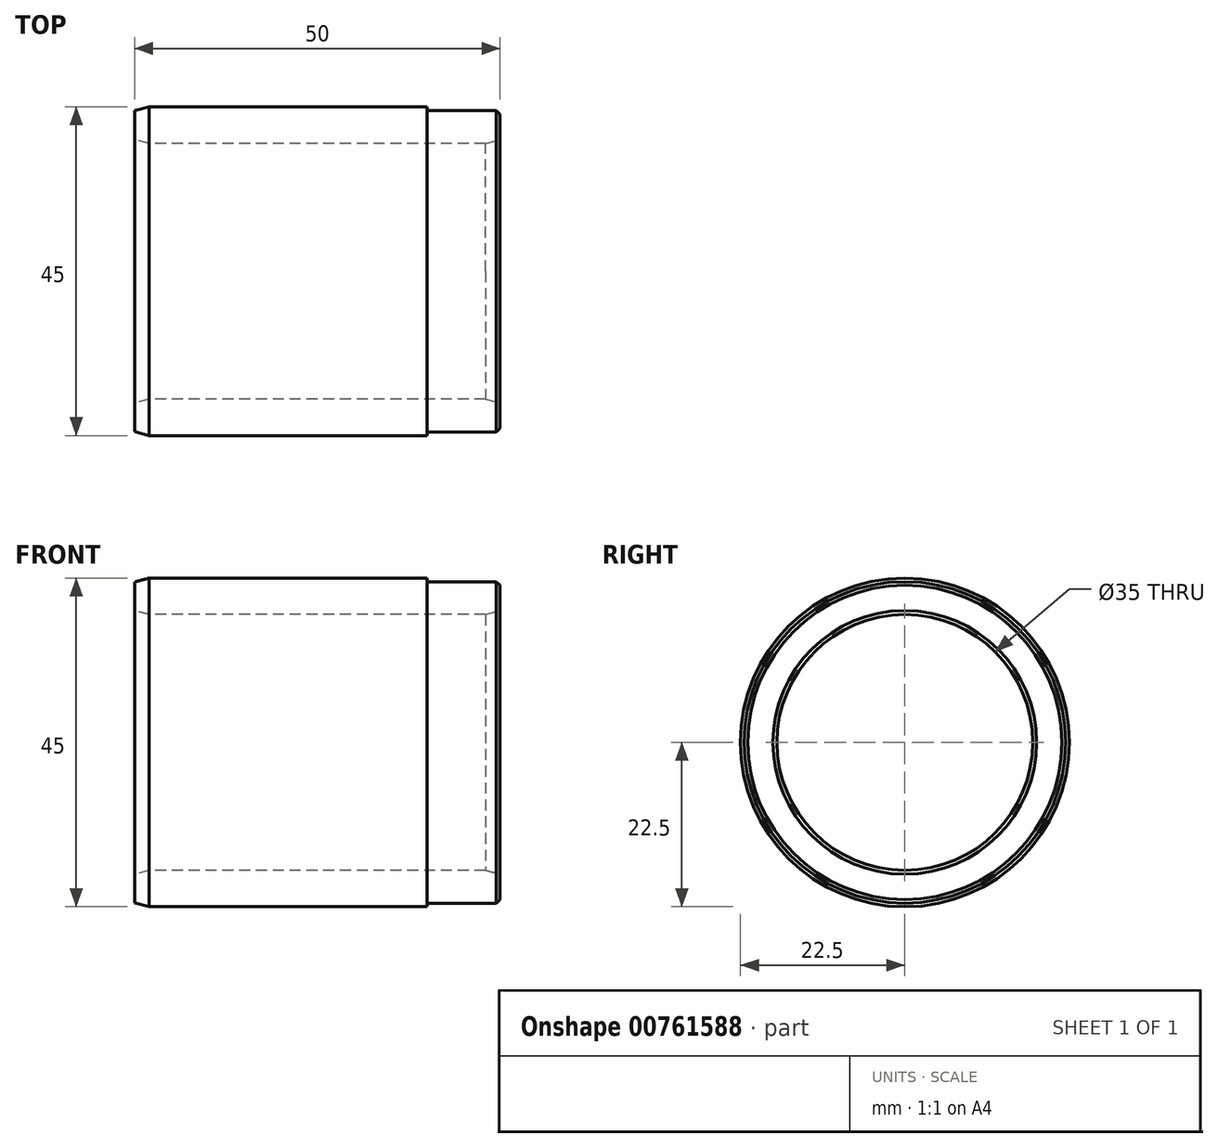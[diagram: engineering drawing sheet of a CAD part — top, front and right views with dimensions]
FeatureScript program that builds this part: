
annotation { "Feature Type Name" : "Feature", "Feature Type Description" : "" }
export const myFeature = defineFeature(function(context is Context, id is Id, definition is map)
    precondition{}
    {
        {
            var Q0;
            Q0=qCreatedBy(makeId("Front.planeOp"),FACE);
            var sketch = newSketch(context, id + "F0", { "sketchPlane" : qUnion([Q0])});
            skLineSegment(sketch, "E0", {"start": v(0, 17.5) * mm, "end": v(0, 22.5) * mm});
            skLineSegment(sketch, "E1", {"start": v(0, 22.5) * mm, "end": v(40, 22.5) * mm});
            skLineSegment(sketch, "E2", {"start": v(40, 22.5) * mm, "end": v(40, 22) * mm});
            skLineSegment(sketch, "E3", {"start": v(40, 22) * mm, "end": v(50, 22) * mm});
            skLineSegment(sketch, "E4", {"start": v(50, 22) * mm, "end": v(50, 17.5) * mm});
            skLineSegment(sketch, "E5", {"start": v(0, 17.5) * mm, "end": v(50, 17.5) * mm});
            skLineSegment(sketch, "E6", {"start": v(0, 0) * mm, "end": v(50, 0) * mm, "construction": true});
            skSolve(sketch);
        }
        {
            var Q0;
            Q0=makeQuery(id+"F0.imprint","IMPRINT",FACE,{"disambiguationData":[TD([[makeQuery(id+"F0.imprint","IMPRINT",EDGE,{"derivedFrom":sQuery(id+"F0.wireOp",EDGE,"E0")}),-1.0]])]});
            var Q1;
            Q1=sQuery(id+"F0.wireOp",EDGE,"E6");
            revolve(context, id + "F1", {"surfaceOperationType" : NewSurfaceOperationType.NEW, "entities" : qUnion([Q0]), "axis" : qUnion([Q1]), "revolveType" : RevolveType.FULL});
        }
        {
            var Q0;
            Q0=makeQuery(id+"F1.opRevolve","SWEPT_EDGE",EDGE,{"disambiguationData":[OSD([sQuery(id+"F0.wireOp",EDGE,"E0"),sQuery(id+"F0.wireOp",EDGE,"E1")])]});
            var Q1;
            Q1=makeQuery(id+"F1.opRevolve","SWEPT_EDGE",EDGE,{"disambiguationData":[OSD([sQuery(id+"F0.wireOp",EDGE,"E0"),sQuery(id+"F0.wireOp",EDGE,"E5")])]});
            var Q2;
            Q2=makeQuery(id+"F1.opRevolve","SWEPT_EDGE",EDGE,{"disambiguationData":[OSD([sQuery(id+"F0.wireOp",EDGE,"E4"),sQuery(id+"F0.wireOp",EDGE,"E5")])]});
            chamfer(context, id + "F2", {"entities" : qUnion([Q0, Q1, Q2]), "chamferType" : ChamferType.OFFSET_ANGLE, "width" : 2 * mm, "oppositeDirection" : true, "angle" : 15 * degree, "tangentPropagation" : true});
        }
        {
            var Q0;
            Q0=makeQuery(id+"F1.opRevolve","SWEPT_EDGE",EDGE,{"disambiguationData":[OSD([sQuery(id+"F0.wireOp",EDGE,"E3"),sQuery(id+"F0.wireOp",EDGE,"E4")])]});
            chamfer(context, id + "F3", {"entities" : qUnion([Q0]), "width" : 0.5 * mm, "tangentPropagation" : true});
        }
    });
